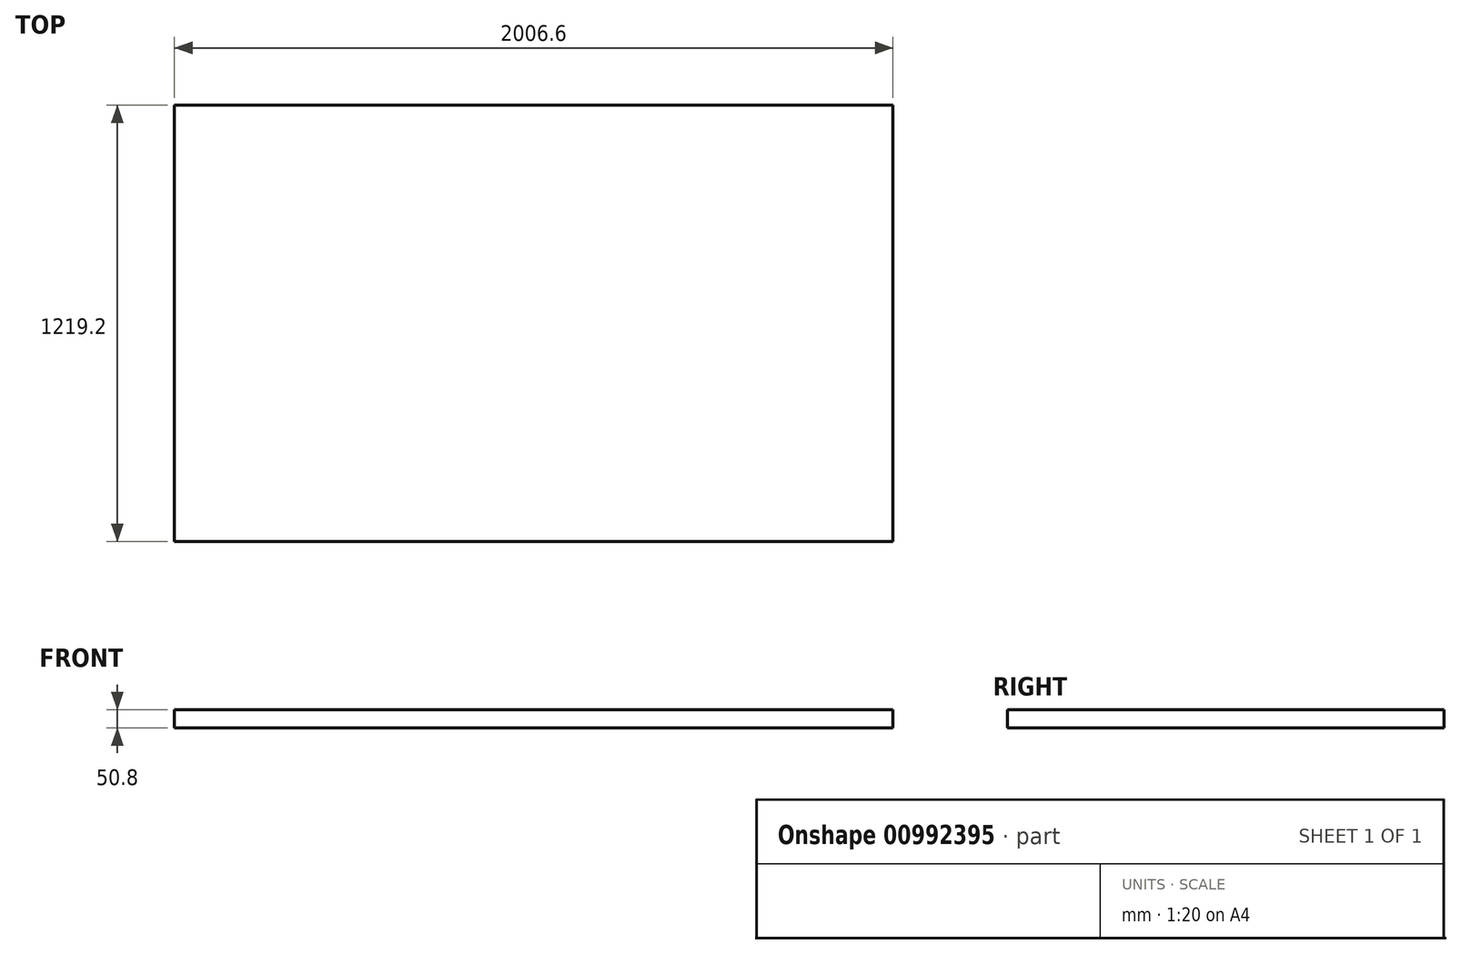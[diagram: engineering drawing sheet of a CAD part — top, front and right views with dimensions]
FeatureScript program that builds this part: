
annotation { "Feature Type Name" : "Feature", "Feature Type Description" : "" }
export const myFeature = defineFeature(function(context is Context, id is Id, definition is map)
    precondition{}
    {
        {
            var Q0;
            Q0=qCreatedBy(makeId("Front.planeOp"),FACE);
            var sketch = newSketch(context, id + "F0", { "sketchPlane" : qUnion([Q0])});
            skLineSegment(sketch, "E0.bottom", {"start": v(1003.3, 25.4) * mm, "end": v(-1003.3, 25.4) * mm});
            skLineSegment(sketch, "E0.top", {"start": v(1003.3, -25.4) * mm, "end": v(-1003.3, -25.4) * mm});
            skLineSegment(sketch, "E0.left", {"start": v(1003.3, 25.4) * mm, "end": v(1003.3, -25.4) * mm});
            skLineSegment(sketch, "E0.right", {"start": v(-1003.3, 25.4) * mm, "end": v(-1003.3, -25.4) * mm});
            skPoint(sketch, "E0.middle", {"position": v(0, 0) * mm});
            skSolve(sketch);
        }
        {
            var Q0;
            Q0=makeQuery(id+"F0.imprint","IMPRINT",FACE,{"disambiguationData":[TD([[makeQuery(id+"F0.imprint","IMPRINT",EDGE,{"derivedFrom":sQuery(id+"F0.wireOp",EDGE,"E0.bottom")}),1.0]])]});
            extrude(context, id + "F1", {"entities" : qUnion([Q0]), "depth" : 1219.2 * mm, "offsetDistance" : 25.4 * mm});
        }
    });
